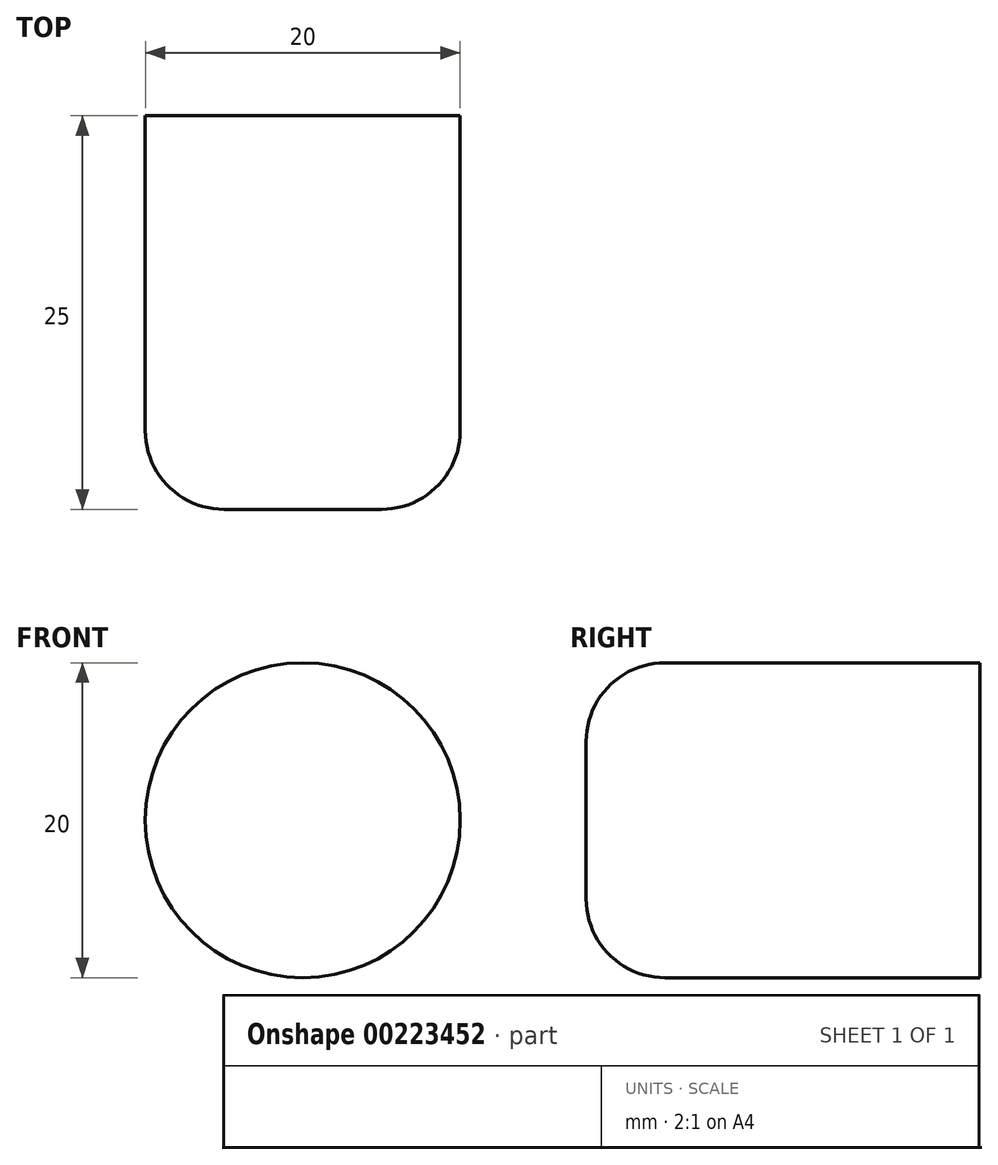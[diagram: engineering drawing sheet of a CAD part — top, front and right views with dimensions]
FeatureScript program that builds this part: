
annotation { "Feature Type Name" : "Feature", "Feature Type Description" : "" }
export const myFeature = defineFeature(function(context is Context, id is Id, definition is map)
    precondition{}
    {
        {
            var Q0;
            Q0=qCreatedBy(makeId("Front.planeOp"),FACE);
            var sketch = newSketch(context, id + "F0", { "sketchPlane" : qUnion([Q0])});
            skLineSegment(sketch, "E0", {"start": v(0, 0) * mm, "end": v(0, 50) * mm});
            skCircle(sketch, "E1", {"center": v(10, 50.24) * mm, "radius": 10 * mm});
            skSolve(sketch);
        }
        {
            var Q0;
            Q0=makeQuery(id+"F0.imprint","IMPRINT",FACE,{"disambiguationData":[TD([[makeQuery(id+"F0.imprint","IMPRINT",EDGE,{"derivedFrom":sQuery(id+"F0.wireOp",EDGE,"E1")}),1.0]])]});
            extrude(context, id + "F1", {"entities" : qUnion([Q0]), "depth" : 25 * mm});
        }
        {
            var Q0;
            Q0=makeQuery(id+"F1.opExtrude","CAP_EDGE",EDGE,{"disambiguationData":[OSD([sQuery(id+"F0.wireOp",EDGE,"E1")])],"isStart":false});
            fillet(context, id + "F2", {"entities" : qUnion([Q0]), "radius" : 5 * mm, "tangentPropagation" : true, "allowEdgeOverflow" : false});
        }
    });
